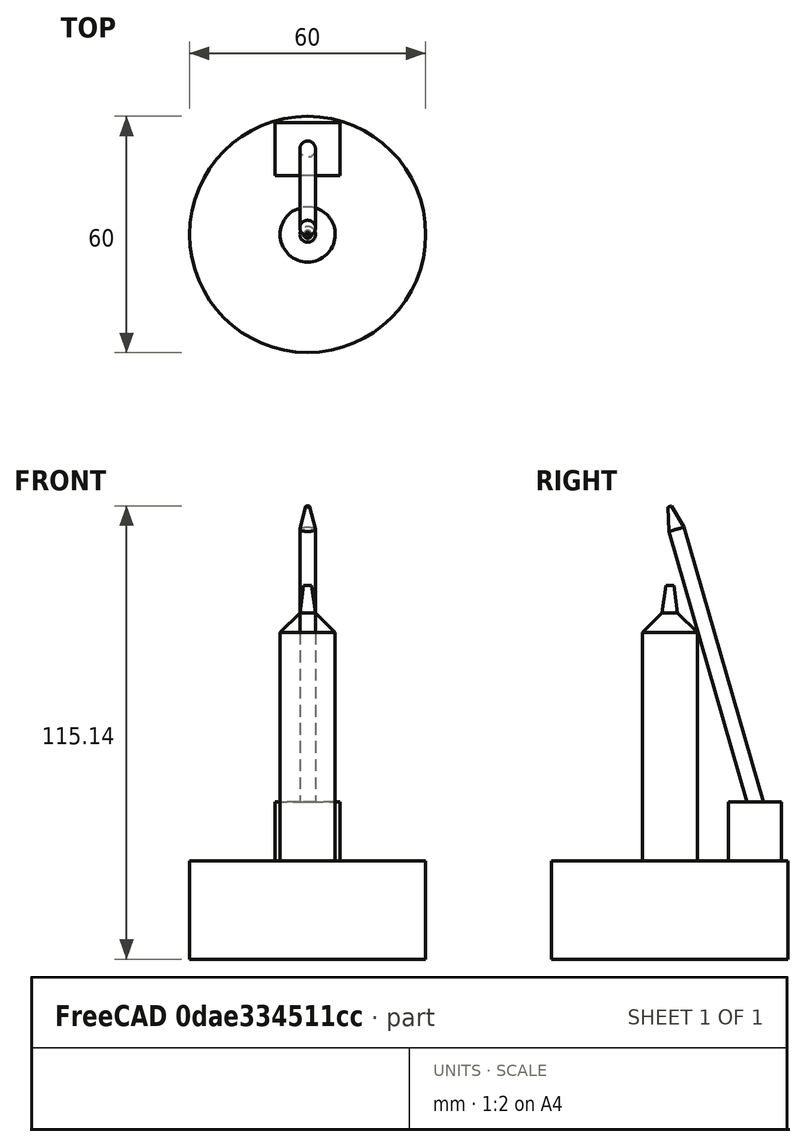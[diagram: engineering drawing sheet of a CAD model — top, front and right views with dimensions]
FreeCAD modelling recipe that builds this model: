
FCSTD DOCUMENT  (FreeCAD 0.19R24366 (Git))
Label: link_6
License: All rights reserved
LicenseURL: http://en.wikipedia.org/wiki/All_rights_reserved
objects: Sketcher::SketchObject×4, PartDesign::Pad×2, PartDesign::Revolution×2, PartDesign::Body×1, Mesh::Feature×1
note: 13 computed .brp shape members not serialized (recipe doc carries the construction recipe); baked Part::Feature solids carry a one-line shape summary decoded from their .brp

FEATURE [Sketcher::SketchObject] Sketch001
  FullyConstrained = true
  MapMode = 5
  Placement = pos=(0,0,0) rot=(1,0,0;1.5708rad)
  Support = -> [XZ_Plane]
  sketch-geometry (6):
    g0: LineSegment StartX=7 StartY=0 StartZ=0 EndX=7 EndY=58 EndZ=0
    g1: LineSegment StartX=7 StartY=58 StartZ=0 EndX=2 EndY=63 EndZ=0
    g2: LineSegment StartX=7 StartY=0 StartZ=0 EndX=0 EndY=0 EndZ=0
    g3: LineSegment StartX=2 StartY=63 StartZ=0 EndX=1 EndY=70 EndZ=0
    g4: LineSegment StartX=1 StartY=70 StartZ=0 EndX=0 EndY=70 EndZ=0
    g5: LineSegment StartX=0 StartY=70 StartZ=0 EndX=0 EndY=0 EndZ=0
  constraints (18):
    c: PointOnObject(g0,g-1)
    c: Vertical(g0)
    c: Coincident(g1,g0)
    c: PointOnObject(g2,g-1)
    c: Coincident(g2,g0)
    c: DistanceX(g2,g2) = 7
    c: DistanceY(g0,g1) = 5
    c: Coincident(g3,g1)
    c: Coincident(g4,g3)
    c: PointOnObject(g4,g-2)
    c: Coincident(g5,g4)
    c: Coincident(g5,g2)
    c: Vertical(g5)
    c: DistanceX(g4,g4) = 1
    c: DistanceY(g1,g3) = 7
    c: Horizontal(g4)
    c: DistanceY(g2,g4) = 70
    c: DistanceX(g4,g1) = 2
FEATURE [Sketcher::SketchObject] Sketch
  FullyConstrained = true
  MapMode = 5
  Support = -> [XY_Plane]
  sketch-geometry (1):
    g0: Circle CenterX=0 CenterY=0 CenterZ=0 NormalX=0 NormalY=0 NormalZ=1 AngleXU=0 Radius=30
  constraints (2):
    c: Coincident(g0,g-1)
    c: Diameter(g0) = 60
FEATURE [PartDesign::Pad] Pad
  AllowMultiFace = false
  Direction = (1,1,1)
  Length = 25
  Length2 = 100
  Profile = -> Sketch
  Reversed = true
  Type = 0
FEATURE [PartDesign::Revolution] Revolution
  Angle = 360
  Axis = (0,-2e-16,1)
  Base = (0,0,0)
  BaseFeature = -> Pad
  Profile = -> Sketch001
  ReferenceAxis = -> Sketch001 [V_Axis]
  Reversed = true
FEATURE [Sketcher::SketchObject] Sketch002
  FullyConstrained = false
  MapMode = 5
  Placement = pos=(0,0,0) rot=(0.57735,0.57735,0.57735;2.0944rad)
  Support = -> [YZ_Plane]
  sketch-geometry (6):
    g0: LineSegment StartX=26 StartY=0 StartZ=0 EndX=0 EndY=90 EndZ=0
    g1: LineSegment StartX=0 StartY=90 StartZ=0 EndX=0.480357 EndY=90.1388 EndZ=0
    g2: LineSegment StartX=0.480357 StartY=90.1388 StartZ=0 EndX=3.5906 EndY=84.7772 EndZ=0
    g3: LineSegment StartX=3.5906 StartY=84.7772 StartZ=0 EndX=28.0818 EndY=0 EndZ=0
    g4: LineSegment StartX=28.0818 StartY=0 StartZ=0 EndX=26 EndY=0 EndZ=0
    g5: LineSegment StartX=-6.34722 StartY=111.971 StartZ=0 EndX=32.0551 EndY=-20.96 EndZ=0
  constraints (15):
    c: PointOnObject(g0,g-1)
    c: DistanceY(g-1,g0) = 90
    c: PointOnObject(g0,g-2)
    c: Coincident(g1,g0)
    c: Coincident(g2,g1)
    c: Coincident(g3,g2)
    c: PointOnObject(g3,g-1)
    c: Coincident(g4,g3)
    c: Coincident(g4,g0)
    c: Parallel(g0,g3)
    c: Perpendicular(g0,g1)
    c: Distance(g1) = 0.5
    c: Distance(g2,g0) = 2
    c: Tangent(g5,g0)
    c: DistanceX(g-1,g0) = 26
FEATURE [PartDesign::Revolution] Revolution001
  Angle = 360
  Axis = (4.23e-14,38.4023,-132.931)
  Base = (-2.7e-14,-6.34722,111.971)
  BaseFeature = -> Revolution
  Profile = -> Sketch002
  ReferenceAxis = -> Sketch002 [Axis0]
FEATURE [Sketcher::SketchObject] Sketch003
  ExternalGeometry = -> [Revolution001]
  FullyConstrained = false
  MapMode = 5
  Support = -> [Revolution001]
  sketch-geometry (4):
    g0: LineSegment StartX=-8.26962 StartY=28.3752 StartZ=0 EndX=8.26962 EndY=28.3752 EndZ=0
    g1: LineSegment StartX=8.26962 StartY=28.3752 StartZ=0 EndX=8.26962 EndY=14.8828 EndZ=0
    g2: LineSegment StartX=8.26962 StartY=14.8828 StartZ=0 EndX=-8.26962 EndY=14.8828 EndZ=0
    g3: LineSegment StartX=-8.26962 StartY=14.8828 StartZ=0 EndX=-8.26962 EndY=28.3752 EndZ=0
  constraints (8):
    c: Coincident(g0,g1)
    c: Coincident(g1,g2)
    c: Coincident(g2,g3)
    c: Coincident(g3,g0)
    c: Horizontal(g2)
    c: Vertical(g1)
    c: Vertical(g3)
    c: Symmetric(g0,g0,g-2)
FEATURE [PartDesign::Pad] Pad001
  BaseFeature = -> Revolution001
  Direction = (1,1,1)
  Length = 15
  Length2 = 100
  Profile = -> Sketch003
  Type = 0
FEATURE [PartDesign::Body] Body
  Group = -> [Sketch,Pad,Sketch001,Revolution,Sketch002,Revolution001,Sketch003,Pad001]
  Origin = -> Origin
  Placement = pos=(0,0,25) rot=(0,0,1;0rad)
  Tip = -> Pad001
FEATURE [Mesh::Feature] Mesh  label="Body (Meshed)"
